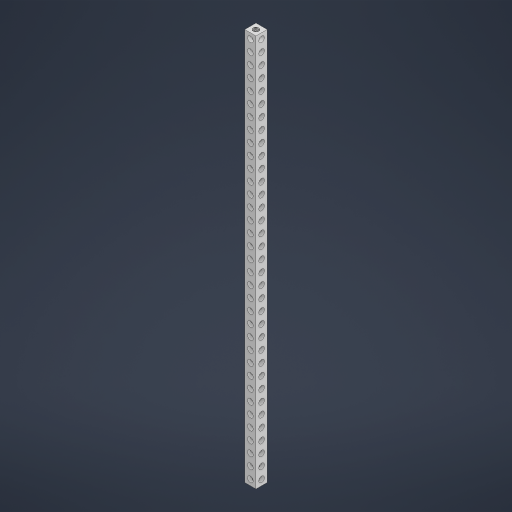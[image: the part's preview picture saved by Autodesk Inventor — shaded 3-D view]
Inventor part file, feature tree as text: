
AUTODESK INVENTOR PART (.ipt)
format: ipt  version: 2023 (Build 270158000, 158)  size: 1,323,520 bytes
history: native  units: in
note: dims shown in document units (in); Inventor stores cm internally (conversion verified against a paired STEP export)
features: mirror x1
ambient origin geometry x8: Origin, YZ Plane, XZ Plane, XY Plane, X Axis, Y Axis, Z Axis, Center Point
bodies: Solid1 (feature_tree)
feature tree (1):
  mirror  "Mirror3"
